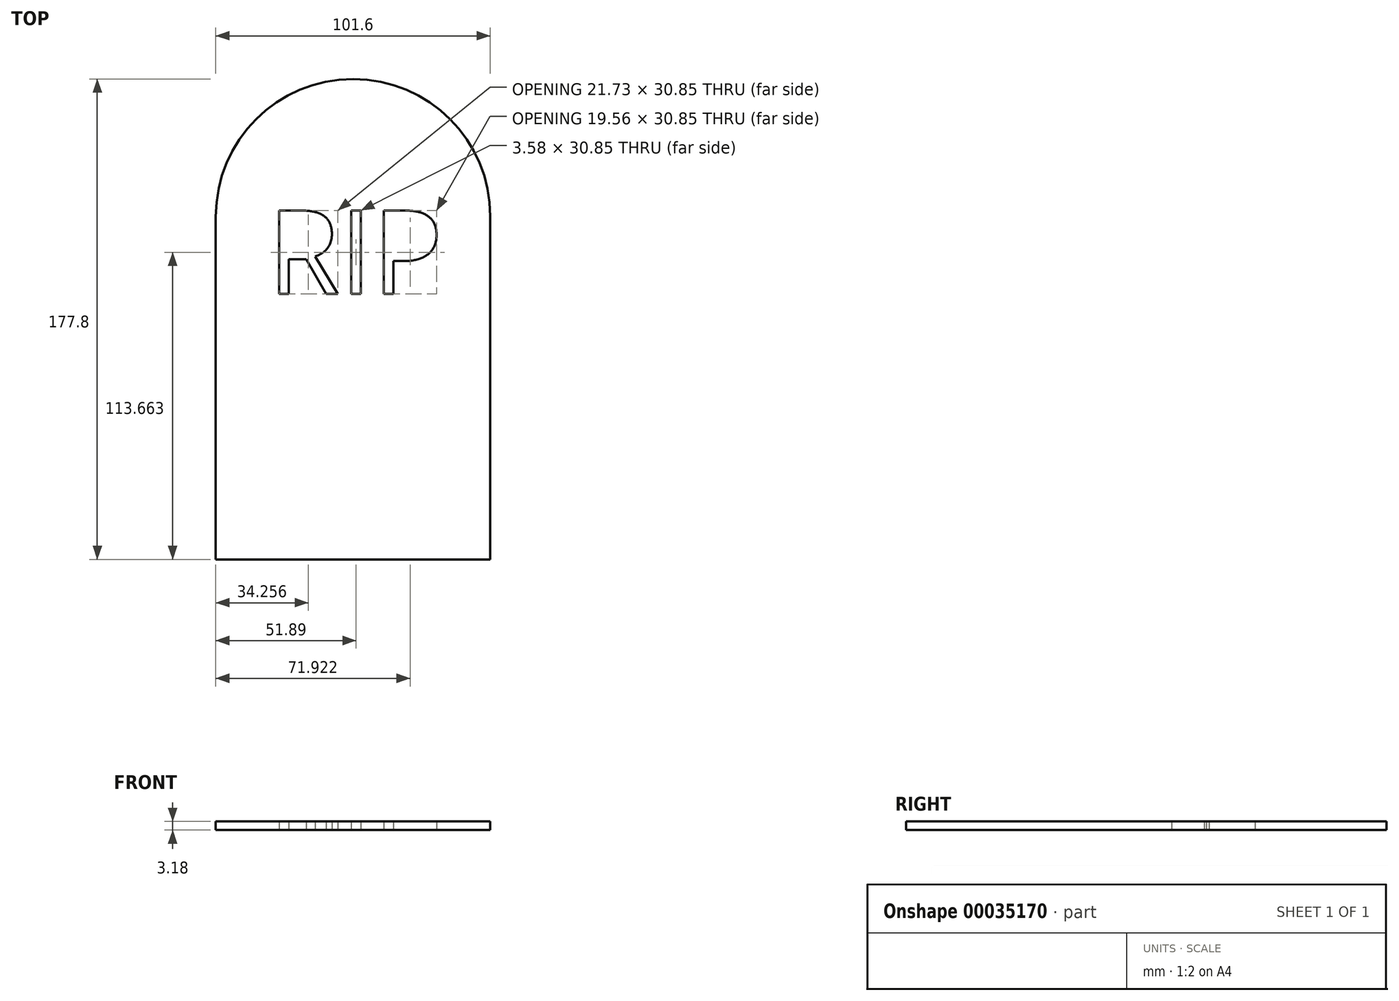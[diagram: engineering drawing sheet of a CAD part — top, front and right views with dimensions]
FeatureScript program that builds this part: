
annotation { "Feature Type Name" : "Feature", "Feature Type Description" : "" }
export const myFeature = defineFeature(function(context is Context, id is Id, definition is map)
    precondition{}
    {
        {
            var Q0;
            Q0=qCreatedBy(makeId("Top.planeOp"),FACE);
            var sketch = newSketch(context, id + "F0", { "sketchPlane" : qUnion([Q0])});
            skLineSegment(sketch, "E0.bottom", {"start": v(-43.65, -69.4) * mm, "end": v(57.95, -69.4) * mm});
            skLineSegment(sketch, "E0.top", {"start": v(-43.65, 57.6) * mm, "end": v(57.95, 57.6) * mm});
            skLineSegment(sketch, "E0.left", {"start": v(-43.65, -69.4) * mm, "end": v(-43.65, 57.6) * mm});
            skLineSegment(sketch, "E0.right", {"start": v(57.95, -69.4) * mm, "end": v(57.95, 57.6) * mm});
            skArc(sketch, "E1", {"start": v(57.95, 57.6) * mm, "mid": v(7.15, 108.4) * mm, "end": v(-43.65, 57.6) * mm});
            skText(sketch, "E2", { "text": "RIP", "fontName": "OpenSans-Regular.ttf"});
            const initialGuessF0  = {"E2": [-0.0245, 0.02885, 1, 0, 0.03111]};
            skSetInitialGuess(sketch, initialGuessF0);
            skSolve(sketch);
        }
        {
            var Q0;
            Q0=makeQuery(id+"F0.imprint","IMPRINT",FACE,{"disambiguationData":[TD([[makeQuery(id+"F0.imprint","IMPRINT",EDGE,{"derivedFrom":sQuery(id+"F0.wireOp",EDGE,"E0.bottom")}),1.0]])]});
            var Q1;
            Q1=makeQuery(id+"F0.imprint","IMPRINT",FACE,{"disambiguationData":[TD([[makeQuery(id+"F0.imprint","IMPRINT",EDGE,{"derivedFrom":sQuery(id+"F0.wireOp",EDGE,"E0.top")}),1.0]])]});
            extrude(context, id + "F1", {"entities" : qUnion([Q0, Q1]), "depth" : 3.17 * mm});
        }
    });
